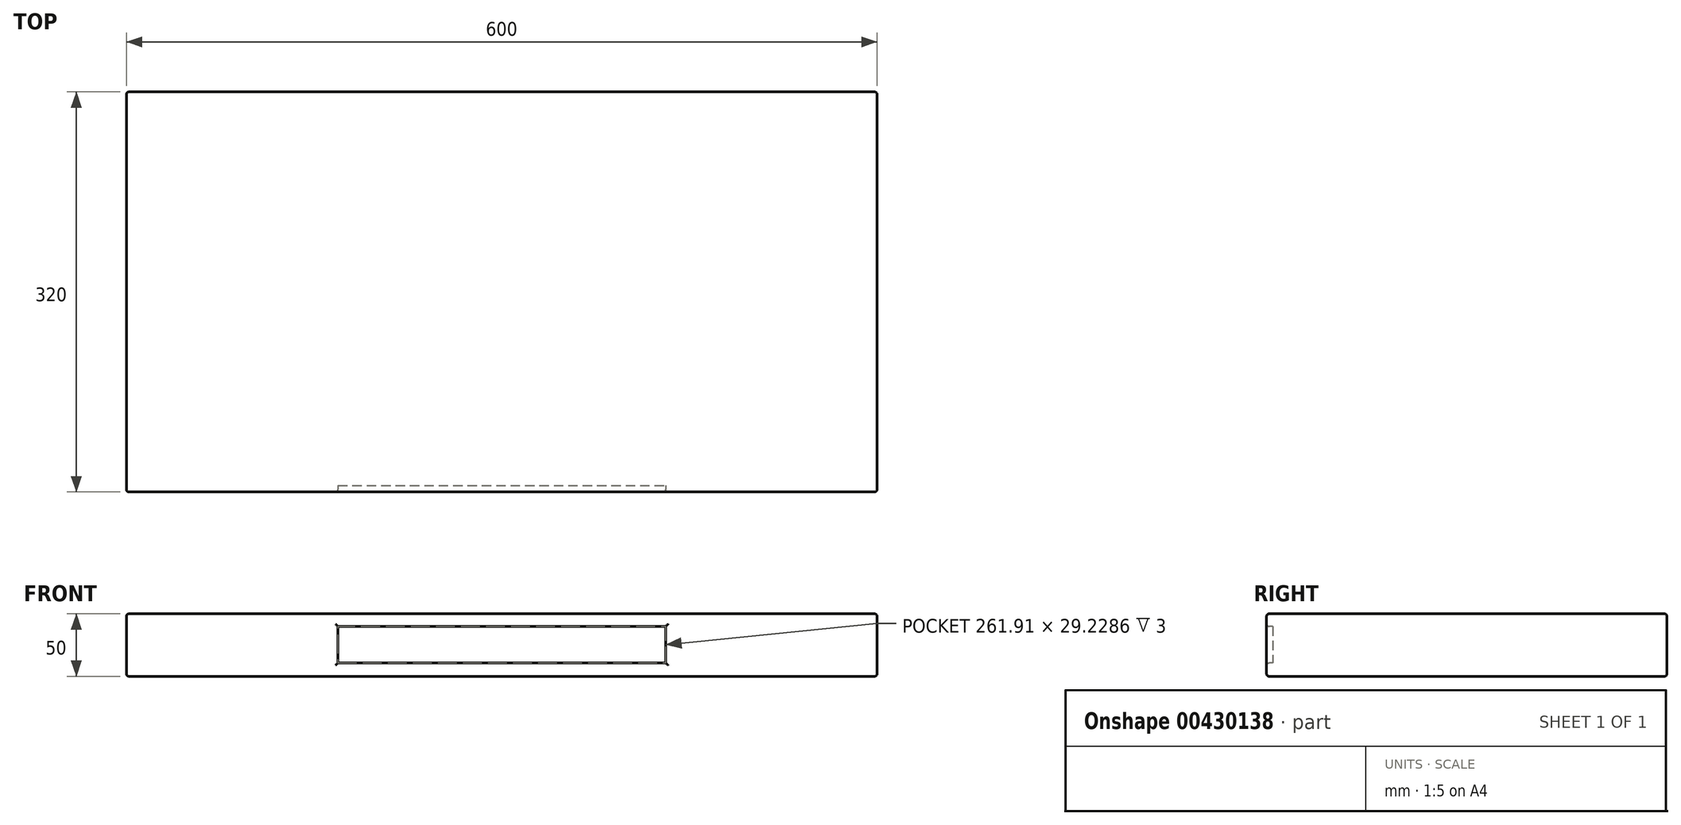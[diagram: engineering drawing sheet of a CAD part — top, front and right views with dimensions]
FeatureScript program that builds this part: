
annotation { "Feature Type Name" : "Feature", "Feature Type Description" : "" }
export const myFeature = defineFeature(function(context is Context, id is Id, definition is map)
    precondition{}
    {
        {
            var Q0;
            Q0=qCreatedBy(makeId("Top.planeOp"),FACE);
            var sketch = newSketch(context, id + "F0", { "sketchPlane" : qUnion([Q0])});
            skLineSegment(sketch, "E0.bottom", {"start": v(0, 0) * mm, "end": v(-54.57, 0) * mm});
            skLineSegment(sketch, "E0.top", {"start": v(0, -50.01) * mm, "end": v(-54.57, -50.01) * mm});
            skLineSegment(sketch, "E0.left", {"start": v(0, 0) * mm, "end": v(0, -50.01) * mm});
            skLineSegment(sketch, "E0.right", {"start": v(-54.57, 0) * mm, "end": v(-54.57, -50.01) * mm});
            skSolve(sketch);
        }
        {
            var Q0;
            Q0=makeQuery(id+"F0.imprint","IMPRINT",FACE,{"disambiguationData":[TD([[makeQuery(id+"F0.imprint","IMPRINT",EDGE,{"derivedFrom":sQuery(id+"F0.wireOp",EDGE,"E0.bottom")}),1.0]])]});
            extrude(context, id + "F1", {"entities" : qUnion([Q0]), "depth" : 50 * mm});
        }
        {
            var Q0;
            Q0=makeQuery(id+"F1.opExtrude","SWEPT_FACE",FACE,{"disambiguationData":[OSD([sQuery(id+"F0.wireOp",EDGE,"E0.left")])]});
            extrude(context, id + "F2", {"entities" : qUnion([Q0]), "operationType" : NewBodyOperationType.ADD, "oppositeDirection" : true, "depth" : 600 * mm});
        }
        {
            var Q0;
            {var subQ0=sQuery(id+"F0.wireOp",EDGE,"E0.bottom");Q0=makeQuery(id+"F2.boolean.opBoolean","MERGE",FACE,{"derivedFrom":[makeQuery(id+"F1.opExtrude","SWEPT_FACE",FACE,{"disambiguationData":[OSD([subQ0])]}),makeQuery(id+"F2.opExtrude","SWEPT_FACE",FACE,{"disambiguationData":[OSD([subQ0,sQuery(id+"F0.wireOp",EDGE,"E0.left")])]})]});}
            extrude(context, id + "F3", {"entities" : qUnion([Q0]), "operationType" : NewBodyOperationType.ADD, "oppositeDirection" : true, "depth" : 320 * mm});
        }
        {
            var Q0;
            Q0=makeQuery(id+"F3.opExtrude","CAP_FACE",FACE,{"disambiguationData":[OSD([sQuery(id+"F0.wireOp",EDGE,"E0.bottom"),sQuery(id+"F0.wireOp",EDGE,"E0.left")])],"isStart":false});
            var sketch = newSketch(context, id + "F4", { "sketchPlane" : qUnion([Q0])});
            skLineSegment(sketch, "E1.bottom", {"start": v(-430.86, 39.93) * mm, "end": v(-168.95, 39.93) * mm});
            skLineSegment(sketch, "E1.top", {"start": v(-430.86, 10.7) * mm, "end": v(-168.95, 10.7) * mm});
            skLineSegment(sketch, "E1.left", {"start": v(-430.86, 39.93) * mm, "end": v(-430.86, 10.7) * mm});
            skLineSegment(sketch, "E1.right", {"start": v(-168.95, 39.93) * mm, "end": v(-168.95, 10.7) * mm});
            skSolve(sketch);
        }
        {
            var Q0;
            Q0=makeQuery(id+"F4.imprint","IMPRINT",FACE,{"disambiguationData":[TD([[makeQuery(id+"F4.imprint","IMPRINT",EDGE,{"derivedFrom":sQuery(id+"F4.wireOp",EDGE,"E1.bottom")}),-1.0]])]});
            extrude(context, id + "F5", {"entities" : qUnion([Q0]), "operationType" : NewBodyOperationType.REMOVE, "oppositeDirection" : true, "depth" : 5 * mm});
        }
        {
            var Q0;
            {var subQ0=sQuery(id+"F0.wireOp",EDGE,"E0.left");var subQ1=sQuery(id+"F0.wireOp",EDGE,"E0.bottom");Q0=makeQuery(id+"F3.boolean.opBoolean","MERGE",FACE,{"derivedFrom":[makeQuery(id+"F2.boolean.opBoolean","MERGE",FACE,{"derivedFrom":[makeQuery(id+"F1.opExtrude","CAP_FACE",FACE,{"disambiguationData":[OSD([subQ1,sQuery(id+"F0.wireOp",EDGE,"E0.top"),subQ0,sQuery(id+"F0.wireOp",EDGE,"E0.right")])],"isStart":false}),makeQuery(id+"F2.opExtrude","SWEPT_FACE",FACE,{"disambiguationData":[OSD([subQ0]),TDD([makeQuery(id+"F1.opExtrude","CAP_EDGE",EDGE,{"disambiguationData":[OSD([subQ0])],"isStart":false})])]})]}),makeQuery(id+"F3.opExtrude","SWEPT_FACE",FACE,{"disambiguationData":[OSD([subQ1,subQ0]),TDD([makeQuery(id+"F2.boolean.opBoolean","MERGE",EDGE,{"derivedFrom":[makeQuery(id+"F1.opExtrude","CAP_EDGE",EDGE,{"disambiguationData":[OSD([subQ1])],"isStart":false}),makeQuery(id+"F2.opExtrude","SWEPT_EDGE",EDGE,{"disambiguationData":[OSD([subQ1,subQ0]),TDD([makeQuery(id+"F1.opExtrude","CAP_VERTEX",VERTEX,{"disambiguationData":[OSD([subQ1,subQ0])],"isStart":false})])]})]})])]})]});}
            var Q1;
            Q1=makeQuery(id+"F3.opExtrude","CAP_FACE",FACE,{"disambiguationData":[OSD([sQuery(id+"F0.wireOp",EDGE,"E0.bottom"),sQuery(id+"F0.wireOp",EDGE,"E0.left")])],"isStart":false});
            var Q2;
            {var subQ0=sQuery(id+"F0.wireOp",EDGE,"E0.left");var subQ1=sQuery(id+"F0.wireOp",EDGE,"E0.bottom");Q2=makeQuery(id+"F3.boolean.opBoolean","MERGE",FACE,{"derivedFrom":[makeQuery(id+"F2.boolean.opBoolean","MERGE",FACE,{"derivedFrom":[makeQuery(id+"F1.opExtrude","CAP_FACE",FACE,{"disambiguationData":[OSD([subQ1,sQuery(id+"F0.wireOp",EDGE,"E0.top"),subQ0,sQuery(id+"F0.wireOp",EDGE,"E0.right")])],"isStart":true}),makeQuery(id+"F2.opExtrude","SWEPT_FACE",FACE,{"disambiguationData":[OSD([subQ0]),TDD([makeQuery(id+"F1.opExtrude","CAP_EDGE",EDGE,{"disambiguationData":[OSD([subQ0])],"isStart":true})])]})]}),makeQuery(id+"F3.opExtrude","SWEPT_FACE",FACE,{"disambiguationData":[OSD([subQ1,subQ0]),TDD([makeQuery(id+"F2.boolean.opBoolean","MERGE",EDGE,{"derivedFrom":[makeQuery(id+"F1.opExtrude","CAP_EDGE",EDGE,{"disambiguationData":[OSD([subQ1])],"isStart":true}),makeQuery(id+"F2.opExtrude","SWEPT_EDGE",EDGE,{"disambiguationData":[OSD([subQ1,subQ0]),TDD([makeQuery(id+"F1.opExtrude","CAP_VERTEX",VERTEX,{"disambiguationData":[OSD([subQ1,subQ0])],"isStart":true})])]})]})])]})]});}
            var Q3;
            {var subQ0=sQuery(id+"F0.wireOp",EDGE,"E0.left");var subQ1=sQuery(id+"F0.wireOp",EDGE,"E0.bottom");Q3=makeQuery(id+"F3.boolean.opBoolean","MERGE",FACE,{"derivedFrom":[makeQuery(id+"F2.opExtrude","CAP_FACE",FACE,{"disambiguationData":[OSD([subQ0])],"isStart":false}),makeQuery(id+"F3.opExtrude","SWEPT_FACE",FACE,{"disambiguationData":[OSD([subQ1,subQ0]),TDD([makeQuery(id+"F2.opExtrude","CAP_EDGE",EDGE,{"disambiguationData":[OSD([subQ1,subQ0])],"isStart":false})])]})]});}
            var Q4;
            {var subQ0=sQuery(id+"F0.wireOp",EDGE,"E0.bottom");Q4=makeQuery(id+"F2.boolean.opBoolean","MERGE",FACE,{"derivedFrom":[makeQuery(id+"F1.opExtrude","SWEPT_FACE",FACE,{"disambiguationData":[OSD([subQ0])]}),makeQuery(id+"F2.opExtrude","SWEPT_FACE",FACE,{"disambiguationData":[OSD([subQ0,sQuery(id+"F0.wireOp",EDGE,"E0.left")])]})]});}
            var Q5;
            {var subQ0=sQuery(id+"F0.wireOp",EDGE,"E0.left");var subQ1=sQuery(id+"F0.wireOp",EDGE,"E0.bottom");Q5=makeQuery(id+"F3.boolean.opBoolean","MERGE",FACE,{"derivedFrom":[makeQuery(id+"F1.opExtrude","SWEPT_FACE",FACE,{"disambiguationData":[OSD([subQ0])]}),makeQuery(id+"F3.opExtrude","SWEPT_FACE",FACE,{"disambiguationData":[OSD([subQ1,subQ0]),TDD([makeQuery(id+"F1.opExtrude","SWEPT_EDGE",EDGE,{"disambiguationData":[OSD([subQ1,subQ0])]})])]})]});}
            fillet(context, id + "F6", {"entities" : qUnion([Q0, Q1, Q2, Q3, Q4, Q5]), "radius" : 2 * mm, "tangentPropagation" : true, "allowEdgeOverflow" : false});
        }
    });
